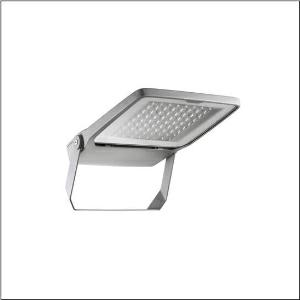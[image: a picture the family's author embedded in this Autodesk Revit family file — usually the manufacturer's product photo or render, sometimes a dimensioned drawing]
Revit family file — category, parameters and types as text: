
# Revit family: floodlight_fl_20_mini___pl43_5xa7672c2a1ac_cb7d
name_source: partatom
category: Lighting Fixtures
units: mm (PartAtom-declared; Revit-internal decimal feet)

## family parameters
Cut with Voids When Loaded = No
Host = Face
Light Source = No
Part Type = Normal
Room Calculation Point = No
Round Connector Dimension = Use Diameter
Shared = No

## types (1)
- --- (1 x LED 4000K / CRI = 70 (unbekannt), 13030 lm, 4000K)
    Apparent Load = 96 VA
    CIE Flux Codes = 32 74 99 100 100
    Color Rendering = 70
    Color Temperature = 4000K
    Default Elevation = 1800 mm
    Description = Floodlight FL 20 mini, floodlight, primary light control with lens, of plastic, primary optical cover: protective disc, of toughened safety glass, transparent, light distribution: PL43, light emission: direct distribution, primary light characteristic: asymmetric, installation type: surface-mounted, LED, High Power LED, rated luminous flux: 13.030lm, luminous efficacy: 136lm/W, light colour: 740, colour temperature: 4000K, control gear: ECG Plus, control: flexible luminous flux parameterisation, time-dependent luminous flux control, digital communication interface, power reduction, overheat protection, electronic power reduction, with terminal, 5-pole, max. 2.5mm², mains connection: 220..240V, AC, 50/60Hz, rated input power: 96W, LED unit, of diecast aluminium, powder-coated, Siteco® metallic grey (DB 702S), corrosivity category C5 mid according to DIN EN ISO 12944, incl. 1x M20 cable gland for cable Ø 6.5..12mm, length: 446mm, width: 355mm, height: 62mm, housing frame, of diecast aluminium, powder-coated, Siteco® metallic grey (DB 702S), mounting bracket, of steel, powder-coated, Siteco® metallic grey (DB 702S), DALI, protection rating (complete): IP66, insulation class (complete): insulation class II (safety insulation), certification: CE, ENEC, VDE, protection symbol: D, permissible operating ambient temperature: -40..+40°C, permissible operating ambient temperature for outdoor applications: -40..+50°C, standard: DIN EN 12944, packaging unit: 1 piece

Light Distribution: PL43
    Height = 62 mm  [stored 0.203412 ft]
    Lamp = 1 x LED 4000K / CRI >= 70 (unbekannt)
    Lamp Light Flux = 13030 lm
    Lamp count = 1
    Length = 467 mm
    Luminous efficacy = 136 lm/W
    Manufacturer = Siteco
    ModVariant = No
    Model = 5XA7672C2A1AC
    Mounting Place = Wall
    Mounting Type = Surface mounted
    Number of Poles = 1
    OnlyDefault = Yes
    Power Factor = 1
    Product Name = Floodlight FL 20 mini | PL43
    Product group = floodlight | wall mounted
    ProductGroupID = 2001
    Protection Class = Protection class II
    Protection Degree = IP 66
    RLX_Detail_Level = 1
    RLX_Emergency_Light_Flux = 0 lm
    RLX_Emergency_Type = 0
    RLX_Emergency_Type_DB = No
    RlxData = <blob elided: 74153 chars, md5=45cf75f6>
    Socket = socket
    Standby Power = 0 W
    System Light Flux = 13030 lm
    System Power = 96 W
    Type Comments = factory setting: luminous flux: 100 % | dim-lin: 254 | 500 mA
    Type Image = l_1005948.jpg
    URL = http://relux.com
    VarID = @adj_164321
    Voltage = 0 V
    Weight = 0.00 kg
    Width = 335 mm

note: [stored X ft] marks values corroborated as IEEE doubles in the binary element streams (Revit-internal decimal feet)

## geometry (parser evidence)
native form markers: Blend x4, Sweep x12
no freeform markers — native parametric forms only
